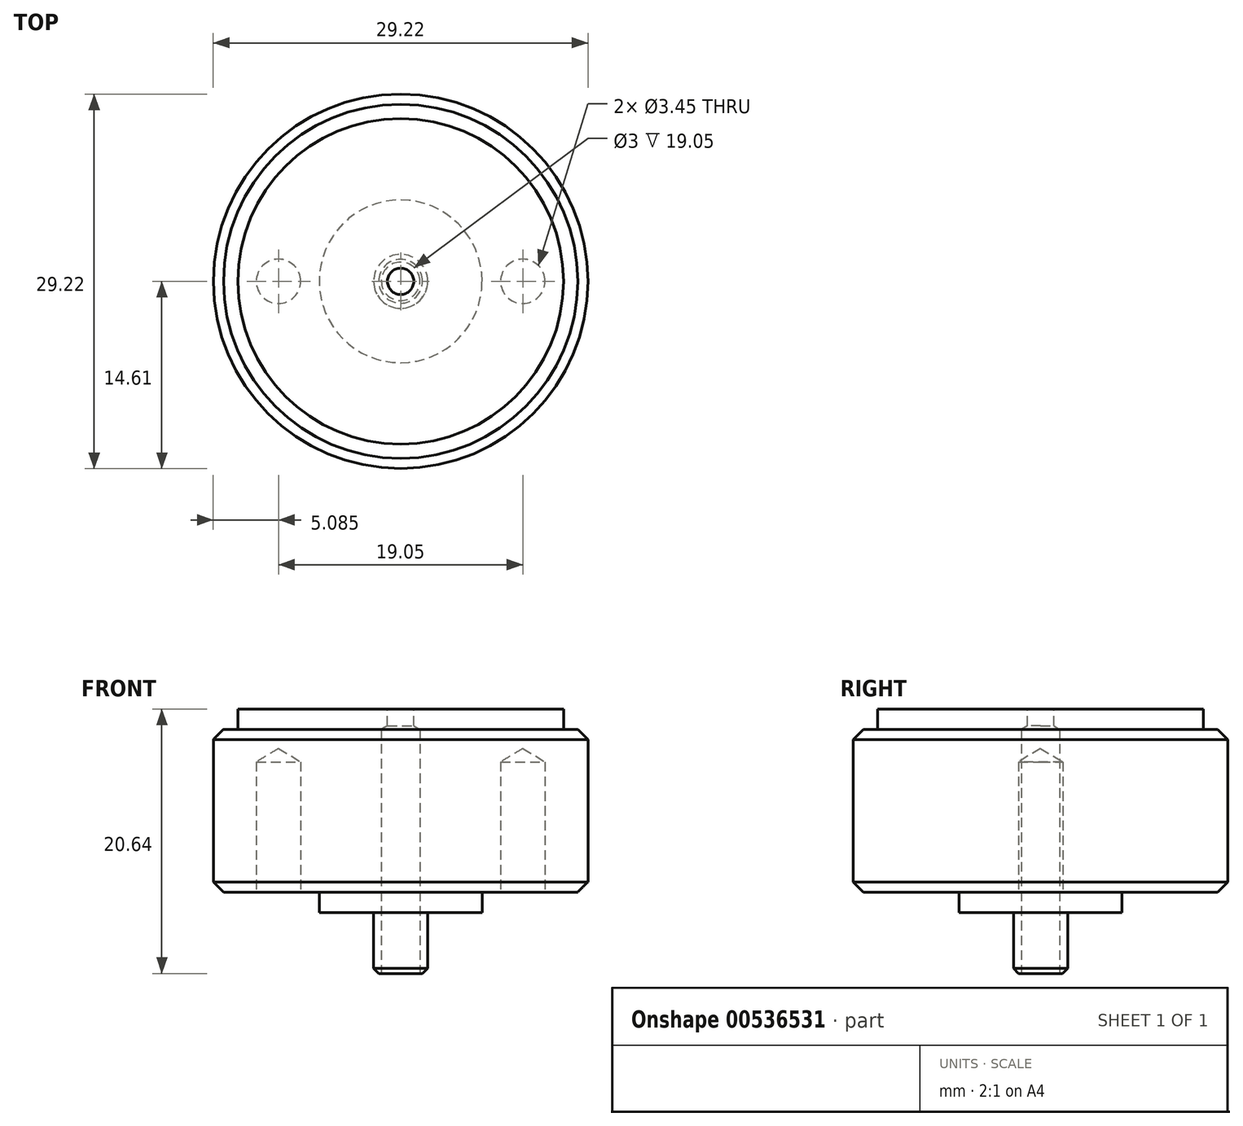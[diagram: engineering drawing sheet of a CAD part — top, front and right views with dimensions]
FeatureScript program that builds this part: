
annotation { "Feature Type Name" : "Feature", "Feature Type Description" : "" }
export const myFeature = defineFeature(function(context is Context, id is Id, definition is map)
    precondition{}
    {
        {
            var Q0;
            Q0=qCreatedBy(makeId("Front.planeOp"),FACE);
            var sketch = newSketch(context, id + "F0", { "sketchPlane" : qUnion([Q0])});
            skLineSegment(sketch, "E0", {"start": v(0, 0) * mm, "end": v(12.7, 0) * mm});
            skLineSegment(sketch, "E1", {"start": v(12.7, 0) * mm, "end": v(12.7, -1.59) * mm});
            skLineSegment(sketch, "E2", {"start": v(12.7, -1.59) * mm, "end": v(14.6, -1.59) * mm});
            skLineSegment(sketch, "E3", {"start": v(14.6, -1.59) * mm, "end": v(14.6, -14.29) * mm});
            skLineSegment(sketch, "E4", {"start": v(14.6, -14.29) * mm, "end": v(6.35, -14.29) * mm});
            skLineSegment(sketch, "E5", {"start": v(2.1, -15.87) * mm, "end": v(2.1, -20.64) * mm});
            skLineSegment(sketch, "E6", {"start": v(2.1, -20.64) * mm, "end": v(0, -20.64) * mm});
            skLineSegment(sketch, "E7", {"start": v(0, -20.64) * mm, "end": v(0, 0) * mm});
            skLineSegment(sketch, "E8", {"start": v(6.35, -14.29) * mm, "end": v(6.35, -15.87) * mm});
            skLineSegment(sketch, "E9", {"start": v(6.35, -15.87) * mm, "end": v(2.1, -15.87) * mm});
            skSolve(sketch);
        }
        {
            var Q0;
            Q0 = qSketchRegion(id + "F0", true);
            var Q1;
            Q1=sQuery(id+"F0.wireOp",EDGE,"E7");
            revolve(context, id + "F1", {"entities" : qUnion([Q0]), "axis" : qUnion([Q1]), "revolveType" : RevolveType.FULL});
        }
        {
            var Q0;
            Q0=makeQuery(id+"F1.opRevolve","SWEPT_FACE",FACE,{"disambiguationData":[OSD([sQuery(id+"F0.wireOp",EDGE,"E0")])]});
            var sketch = newSketch(context, id + "F2", { "sketchPlane" : qUnion([Q0])});
            skPoint(sketch, "E10", {"position": v(0, 0) * mm});
            skSolve(sketch);
        }
        {
            var Q0;
            Q0=sQuery(id+"F2.wireOp",VERTEX,"E10");
            var Q1;
            Q1=makeQuery(id+"F1.opRevolve","SWEPT_BODY",BODY,{"disambiguationData":[OSD([sQuery(id+"F0.wireOp",EDGE,"E0"),sQuery(id+"F0.wireOp",EDGE,"E1"),sQuery(id+"F0.wireOp",EDGE,"E2"),sQuery(id+"F0.wireOp",EDGE,"E3"),sQuery(id+"F0.wireOp",EDGE,"E4"),sQuery(id+"F0.wireOp",EDGE,"E5"),sQuery(id+"F0.wireOp",EDGE,"E6"),sQuery(id+"F0.wireOp",EDGE,"E7")])]});
            hole(context, id + "F3", {"style" : HoleStyle.SIMPLE, "endStyle" : HoleEndStyle.THROUGH, "standardTappedOrClearance" : lookupTablePath({ "standard" : "ANSI", "size" : "#46 (0.08)", "type" : "Drilled" }), "standardBlindInLast" : lookupTablePath({ "standard" : "ANSI", "size" : "#46", "type" : "Drilled" }), "holeDiameter" : 2.06 * mm, "tappedDepth" : 25.4 * mm, "tapClearance" : 3, "startFromSketch" : true, "locations" : qUnion([Q0]), "scope" : qUnion([Q1])});
        }
        {
            var Q0;
            Q0=makeQuery(id+"F1.opRevolve","SWEPT_FACE",FACE,{"disambiguationData":[OSD([sQuery(id+"F0.wireOp",EDGE,"E6")])]});
            var sketch = newSketch(context, id + "F4", { "sketchPlane" : qUnion([Q0])});
            skPoint(sketch, "E11", {"position": v(0, 0) * mm});
            skSolve(sketch);
        }
        {
            var Q0;
            Q0=sQuery(id+"F4.wireOp",VERTEX,"E11");
            var Q1;
            Q1=makeQuery(id+"F1.opRevolve","SWEPT_BODY",BODY,{"disambiguationData":[OSD([sQuery(id+"F0.wireOp",EDGE,"E0"),sQuery(id+"F0.wireOp",EDGE,"E1"),sQuery(id+"F0.wireOp",EDGE,"E2"),sQuery(id+"F0.wireOp",EDGE,"E3"),sQuery(id+"F0.wireOp",EDGE,"E4"),sQuery(id+"F0.wireOp",EDGE,"E5"),sQuery(id+"F0.wireOp",EDGE,"E6"),sQuery(id+"F0.wireOp",EDGE,"E7")])]});
            hole(context, id + "F5", {"style" : HoleStyle.SIMPLE, "endStyle" : HoleEndStyle.BLIND, "standardTappedOrClearance" : lookupTablePath({ "standard" : "ISO", "size" : "3", "type" : "Drilled" }), "standardBlindInLast" : lookupTablePath({ "standard" : "ISO", "size" : "3", "type" : "Drilled" }), "holeDiameter" : 3 * mm, "holeDepth" : 19.05 * mm, "tappedDepth" : 25.4 * mm, "tapClearance" : 3, "startFromSketch" : true, "locations" : qUnion([Q0]), "scope" : qUnion([Q1])});
        }
        {
            var Q0;
            Q0=makeQuery(id+"F1.opRevolve","SWEPT_EDGE",EDGE,{"disambiguationData":[OSD([sQuery(id+"F0.wireOp",EDGE,"E5"),sQuery(id+"F0.wireOp",EDGE,"E6")])]});
            chamfer(context, id + "F6", {"entities" : qUnion([Q0]), "width" : 0.4 * mm, "tangentPropagation" : true});
        }
        {
            var Q0;
            Q0=makeQuery(id+"F1.opRevolve","SWEPT_EDGE",EDGE,{"disambiguationData":[OSD([sQuery(id+"F0.wireOp",EDGE,"E2"),sQuery(id+"F0.wireOp",EDGE,"E3")])]});
            var Q1;
            Q1=makeQuery(id+"F1.opRevolve","SWEPT_EDGE",EDGE,{"disambiguationData":[OSD([sQuery(id+"F0.wireOp",EDGE,"E3"),sQuery(id+"F0.wireOp",EDGE,"E4")])]});
            chamfer(context, id + "F7", {"entities" : qUnion([Q0, Q1]), "width" : 0.8 * mm, "tangentPropagation" : true});
        }
        {
            var Q0;
            Q0=makeQuery(id+"F1.opRevolve","SWEPT_FACE",FACE,{"disambiguationData":[OSD([sQuery(id+"F0.wireOp",EDGE,"E4")])]});
            var sketch = newSketch(context, id + "F8", { "sketchPlane" : qUnion([Q0])});
            skLineSegment(sketch, "E12", {"start": v(-9.53, 0) * mm, "end": v(9.52, 0) * mm, "construction": true});
            skSolve(sketch);
        }
        {
            var Q0;
            Q0=sQuery(id+"F8.wireOp",VERTEX,"E12.start");
            var Q1;
            Q1=sQuery(id+"F8.wireOp",VERTEX,"E12.end");
            var Q2;
            Q2=makeQuery(id+"F1.opRevolve","SWEPT_BODY",BODY,{"disambiguationData":[OSD([sQuery(id+"F0.wireOp",EDGE,"E0"),sQuery(id+"F0.wireOp",EDGE,"E1"),sQuery(id+"F0.wireOp",EDGE,"E2"),sQuery(id+"F0.wireOp",EDGE,"E3"),sQuery(id+"F0.wireOp",EDGE,"E4"),sQuery(id+"F0.wireOp",EDGE,"E5"),sQuery(id+"F0.wireOp",EDGE,"E6"),sQuery(id+"F0.wireOp",EDGE,"E7")])]});
            hole(context, id + "F9", {"style" : HoleStyle.SIMPLE, "endStyle" : HoleEndStyle.BLIND, "standardTappedOrClearance" : lookupTablePath({ "standard" : "ANSI", "engagement" : "75%", "pitch" : "32 tpi", "size" : "#8", "type" : "Tapped" }), "standardBlindInLast" : lookupTablePath({ "standard" : "ANSI", "engagement" : "75%", "pitch" : "32 tpi", "size" : "#8", "type" : "Tapped" }), "holeDiameter" : 3.45 * mm, "showTappedDepth" : true, "holeDepth" : 10.16 * mm, "tappedDepth" : 7.78 * mm, "tapClearance" : 3, "startFromSketch" : true, "locations" : qUnion([Q0, Q1]), "scope" : qUnion([Q2]), "majorDiameter" : 4.17 * mm});
        }
    });
